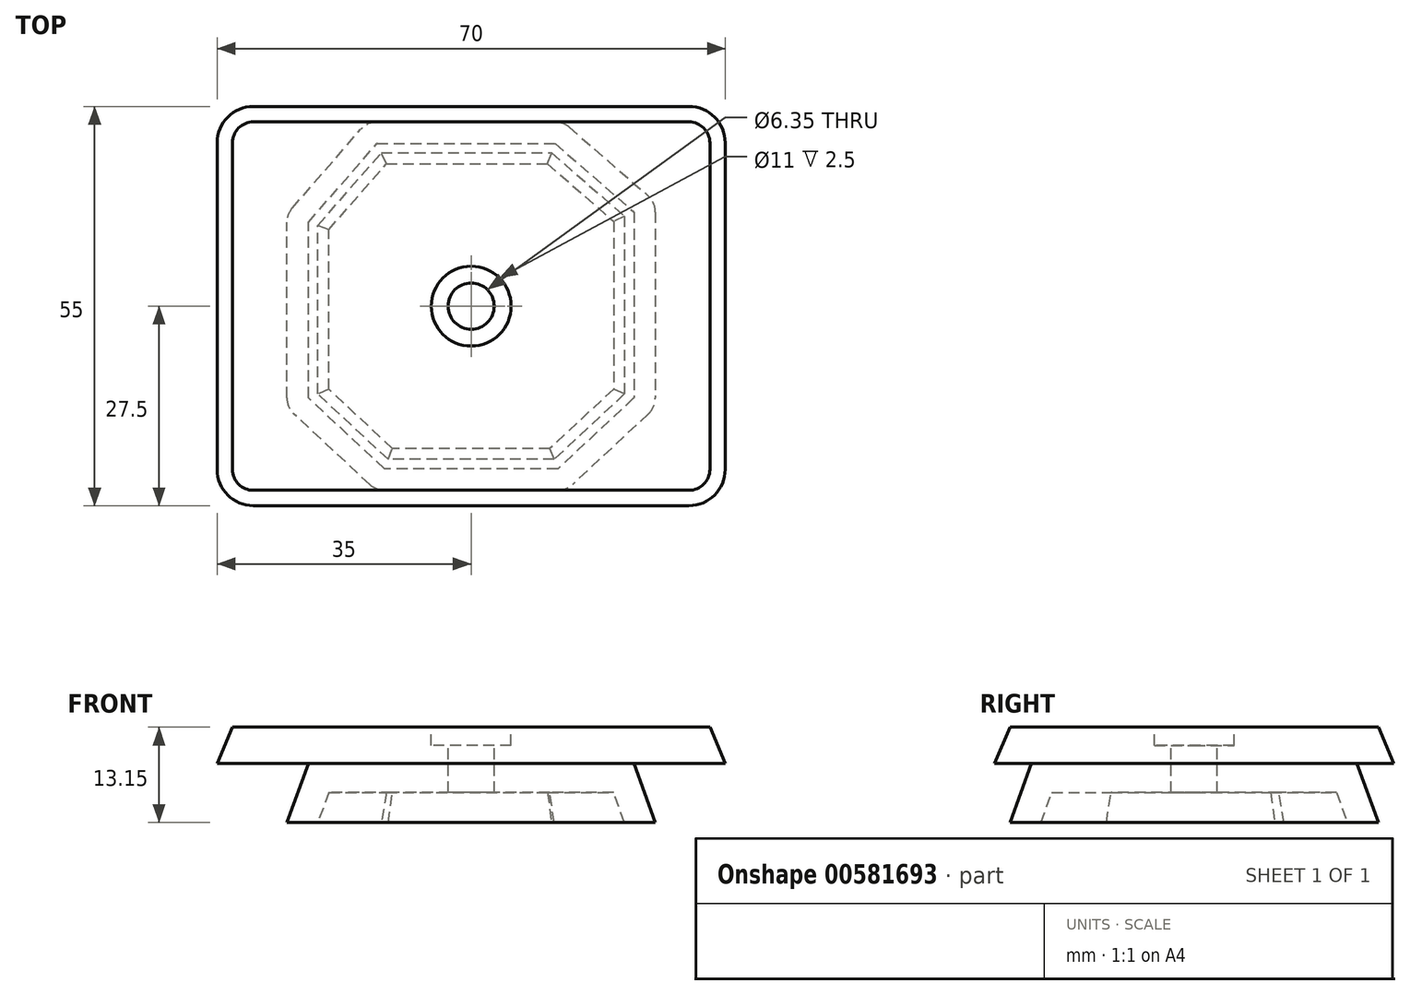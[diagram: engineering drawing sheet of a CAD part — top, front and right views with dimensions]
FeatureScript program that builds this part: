
annotation { "Feature Type Name" : "Feature", "Feature Type Description" : "" }
export const myFeature = defineFeature(function(context is Context, id is Id, definition is map)
    precondition{}
    {
        {
            var Q0;
            Q0=qCreatedBy(makeId("Top.planeOp"),FACE);
            var sketch = newSketch(context, id + "F0", { "sketchPlane" : qUnion([Q0])});
            skLineSegment(sketch, "E0.bottom", {"start": v(11.55, 25.38) * mm, "end": v(-12.96, 25.38) * mm});
            skLineSegment(sketch, "E0.top", {"start": v(11.93, -25.38) * mm, "end": v(-11.93, -25.38) * mm});
            skLineSegment(sketch, "E0.left", {"start": v(25.38, 12.96) * mm, "end": v(25.38, -12.65) * mm});
            skLineSegment(sketch, "E0.right", {"start": v(-25.38, 11.55) * mm, "end": v(-25.38, -12.65) * mm});
            skPoint(sketch, "E0.middle", {"position": v(0, 0) * mm});
            skPoint(sketch, "E1.visualSharp", {"position": v(-25.38, -25.38) * mm});
            skPoint(sketch, "E2.visualSharp", {"position": v(25.38, -25.38) * mm});
            skPoint(sketch, "E3.visualSharp", {"position": v(25.38, 25.38) * mm});
            skPoint(sketch, "E4.visualSharp", {"position": v(-25.38, 25.38) * mm});
            skLineSegment(sketch, "E5", {"start": v(-24.42, -14.85) * mm, "end": v(-13.97, -24.57) * mm});
            skLineSegment(sketch, "E6", {"start": v(13.97, -24.57) * mm, "end": v(24.42, -14.85) * mm});
            skLineSegment(sketch, "E7", {"start": v(24.34, 15.22) * mm, "end": v(13.52, 24.64) * mm});
            skLineSegment(sketch, "E8", {"start": v(-15.22, 24.34) * mm, "end": v(-24.64, 13.52) * mm});
            skPoint(sketch, "E9.visualSharp", {"position": v(-13.1, -25.38) * mm});
            skArc(sketch, "E9.filletArc", {"start": v(-13.97, -24.57) * mm, "mid": v(-13.03, -25.17) * mm, "end": v(-11.93, -25.38) * mm});
            skPoint(sketch, "E10.visualSharp", {"position": v(13.1, -25.38) * mm});
            skArc(sketch, "E10.filletArc", {"start": v(11.93, -25.38) * mm, "mid": v(13.03, -25.17) * mm, "end": v(13.97, -24.57) * mm});
            skPoint(sketch, "E11.visualSharp", {"position": v(25.38, -13.96) * mm});
            skArc(sketch, "E11.filletArc", {"start": v(24.42, -14.85) * mm, "mid": v(25.13, -13.85) * mm, "end": v(25.38, -12.65) * mm});
            skPoint(sketch, "E12.visualSharp", {"position": v(25.38, 14.32) * mm});
            skArc(sketch, "E12.filletArc", {"start": v(25.38, 12.96) * mm, "mid": v(25.1, 14.2) * mm, "end": v(24.34, 15.22) * mm});
            skPoint(sketch, "E13.visualSharp", {"position": v(12.68, 25.38) * mm});
            skArc(sketch, "E13.filletArc", {"start": v(13.52, 24.64) * mm, "mid": v(12.6, 25.18) * mm, "end": v(11.55, 25.38) * mm});
            skPoint(sketch, "E14.visualSharp", {"position": v(-14.32, 25.38) * mm});
            skArc(sketch, "E14.filletArc", {"start": v(-12.96, 25.38) * mm, "mid": v(-14.2, 25.1) * mm, "end": v(-15.22, 24.34) * mm});
            skPoint(sketch, "E15.visualSharp", {"position": v(-25.38, 12.68) * mm});
            skArc(sketch, "E15.filletArc", {"start": v(-24.64, 13.52) * mm, "mid": v(-25.18, 12.6) * mm, "end": v(-25.38, 11.55) * mm});
            skPoint(sketch, "E16.visualSharp", {"position": v(-25.38, -13.96) * mm});
            skArc(sketch, "E16.filletArc", {"start": v(-25.38, -12.65) * mm, "mid": v(-25.13, -13.85) * mm, "end": v(-24.42, -14.85) * mm});
            skSolve(sketch);
        }
        {
            var Q0;
            Q0=makeQuery(id+"F0.imprint","IMPRINT",FACE,{"disambiguationData":[TD([[makeQuery(id+"F0.imprint","IMPRINT",EDGE,{"derivedFrom":sQuery(id+"F0.wireOp",EDGE,"E0.bottom")}),1.0]])]});
            extrude(context, id + "F1", {"entities" : qUnion([Q0]), "depth" : 8.15 * mm, "offsetDistance" : 25 * mm, "hasDraft" : true, "draftAngle" : 20 * degree, "draftPullDirection" : true});
        }
        {
            var Q0;
            Q0=makeQuery(id+"F1.opExtrude","CAP_FACE",FACE,{"disambiguationData":[OSD([sQuery(id+"F0.wireOp",EDGE,"E0.bottom"),sQuery(id+"F0.wireOp",EDGE,"E0.top"),sQuery(id+"F0.wireOp",EDGE,"E0.left"),sQuery(id+"F0.wireOp",EDGE,"E0.right"),sQuery(id+"F0.wireOp",EDGE,"E1.filletArc"),sQuery(id+"F0.wireOp",EDGE,"E2.filletArc"),sQuery(id+"F0.wireOp",EDGE,"E3.filletArc"),sQuery(id+"F0.wireOp",EDGE,"E4.filletArc")])],"isStart":true});
            shell(context, id + "F2", {"entities" : qUnion([Q0]), "thickness" : 4 * mm});
        }
        {
            var Q0;
            Q0=makeQuery(id+"F1.opExtrude","CAP_FACE",FACE,{"disambiguationData":[OSD([sQuery(id+"F0.wireOp",EDGE,"E0.bottom"),sQuery(id+"F0.wireOp",EDGE,"E0.top"),sQuery(id+"F0.wireOp",EDGE,"E0.left"),sQuery(id+"F0.wireOp",EDGE,"E0.right"),sQuery(id+"F0.wireOp",EDGE,"E1.filletArc"),sQuery(id+"F0.wireOp",EDGE,"E2.filletArc"),sQuery(id+"F0.wireOp",EDGE,"E3.filletArc"),sQuery(id+"F0.wireOp",EDGE,"E4.filletArc")])],"isStart":false});
            var sketch = newSketch(context, id + "F3", { "sketchPlane" : qUnion([Q0])});
            skPoint(sketch, "E17.0", {"position": v(0, 0) * mm});
            skLineSegment(sketch, "E18.bottom", {"start": v(30, 27.5) * mm, "end": v(-30, 27.5) * mm});
            skLineSegment(sketch, "E18.top", {"start": v(30, -27.5) * mm, "end": v(-30, -27.5) * mm});
            skLineSegment(sketch, "E18.left", {"start": v(35, 22.5) * mm, "end": v(35, -22.5) * mm});
            skLineSegment(sketch, "E18.right", {"start": v(-35, 22.5) * mm, "end": v(-35, -22.5) * mm});
            skPoint(sketch, "E19.visualSharp", {"position": v(-35, 27.5) * mm});
            skArc(sketch, "E19.filletArc", {"start": v(-30, 27.5) * mm, "mid": v(-33.54, 26.04) * mm, "end": v(-35, 22.5) * mm});
            skPoint(sketch, "E20.visualSharp", {"position": v(35, 27.5) * mm});
            skArc(sketch, "E20.filletArc", {"start": v(35, 22.5) * mm, "mid": v(33.54, 26.04) * mm, "end": v(30, 27.5) * mm});
            skPoint(sketch, "E21.visualSharp", {"position": v(35, -27.5) * mm});
            skArc(sketch, "E21.filletArc", {"start": v(30, -27.5) * mm, "mid": v(33.54, -26.04) * mm, "end": v(35, -22.5) * mm});
            skPoint(sketch, "E22.visualSharp", {"position": v(-35, -27.5) * mm});
            skArc(sketch, "E22.filletArc", {"start": v(-35, -22.5) * mm, "mid": v(-33.54, -26.04) * mm, "end": v(-30, -27.5) * mm});
            skSolve(sketch);
        }
        {
            var Q0;
            Q0=makeQuery(id+"F3.imprint","IMPRINT",FACE,{"disambiguationData":[TD([[makeQuery(id+"F3.imprint","IMPRINT",EDGE,{"derivedFrom":sQuery(id+"F3.wireOp",EDGE,"E18.bottom")}),1.0]])]});
            var Q1;
            Q1=makeQuery(id+"F3.imprint","IMPRINT",FACE,{"disambiguationData":[TD([[makeQuery(id+"F3.imprint","IMPRINT",EDGE,{"derivedFrom":makeQuery(id+"F1.opExtrude","CAP_EDGE",EDGE,{"disambiguationData":[OSD([sQuery(id+"F0.wireOp",EDGE,"E0.bottom")])],"isStart":false})}),1.0]])]});
            extrude(context, id + "F4", {"entities" : qUnion([Q0, Q1]), "operationType" : NewBodyOperationType.ADD, "depth" : 5 * mm, "offsetDistance" : 25 * mm, "hasDraft" : true, "draftAngle" : 23 * degree, "draftPullDirection" : true});
        }
        {
            var Q0;
            Q0=makeQuery(id+"F4.opExtrude","CAP_FACE",FACE,{"disambiguationData":[OSD([sQuery(id+"F3.wireOp",EDGE,"E18.bottom"),sQuery(id+"F3.wireOp",EDGE,"E18.top"),sQuery(id+"F3.wireOp",EDGE,"E18.left"),sQuery(id+"F3.wireOp",EDGE,"E18.right"),sQuery(id+"F3.wireOp",EDGE,"E19.filletArc"),sQuery(id+"F3.wireOp",EDGE,"E20.filletArc"),sQuery(id+"F3.wireOp",EDGE,"E21.filletArc"),sQuery(id+"F3.wireOp",EDGE,"E22.filletArc")])],"isStart":false});
            var sketch = newSketch(context, id + "F5", { "sketchPlane" : qUnion([Q0])});
            skPoint(sketch, "E23.0", {"position": v(0, 0) * mm});
            skSolve(sketch);
        }
        {
            var Q0;
            Q0=sQuery(id+"F5.wireOp",VERTEX,"E23.0");
            var Q1;
            Q1=makeQuery(id+"F1.opExtrude","SWEPT_BODY",BODY,{"disambiguationData":[OSD([sQuery(id+"F0.wireOp",EDGE,"E0.bottom"),sQuery(id+"F0.wireOp",EDGE,"E0.top"),sQuery(id+"F0.wireOp",EDGE,"E0.left"),sQuery(id+"F0.wireOp",EDGE,"E0.right"),sQuery(id+"F0.wireOp",EDGE,"E1.filletArc"),sQuery(id+"F0.wireOp",EDGE,"E2.filletArc"),sQuery(id+"F0.wireOp",EDGE,"E3.filletArc"),sQuery(id+"F0.wireOp",EDGE,"E4.filletArc")])]});
            hole(context, id + "F6", {"style" : HoleStyle.C_BORE, "endStyle" : HoleEndStyle.THROUGH, "holeDiameter" : (25.4 / 4) * mm, "cBoreDiameter" : 11 * mm, "cBoreDepth" : 2.5 * mm, "majorDiameter" : 5 * mm, "isTappedThrough" : true, "tappedDepth" : 12 * mm, "tapClearance" : 3, "locations" : qUnion([Q0]), "scope" : qUnion([Q1])});
        }
    });
